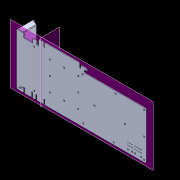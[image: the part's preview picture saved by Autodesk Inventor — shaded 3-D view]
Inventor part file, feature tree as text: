
AUTODESK INVENTOR PART (.ipt)
format: ipt  version: 2018.2 (Build 222227000, 227)  size: 364,544 bytes
history: native  units: mm
features: other x5, imported_body x1, shell x1
ambient origin geometry x8: Origin, YZ Plane, XZ Plane, XY Plane, X Axis, Y Axis, Z Axis, Center Point
bodies: Body1 (feature_tree), Body2 (feature_tree)
feature tree (7):
  other  "修復済みジオメトリ1"
  other  "作業平面1"
  other  "作業平面3"
  other  "ソリッド2"
  imported_body  "Base3"
  shell  "Shell2"  [1 undecoded]
  other  "ソリッド3"
note: 1 required parameter value undecoded (feature->parameter linkage not recoverable at this tier; creation-order binding heuristic only, values carry confidence <= 0.55)
